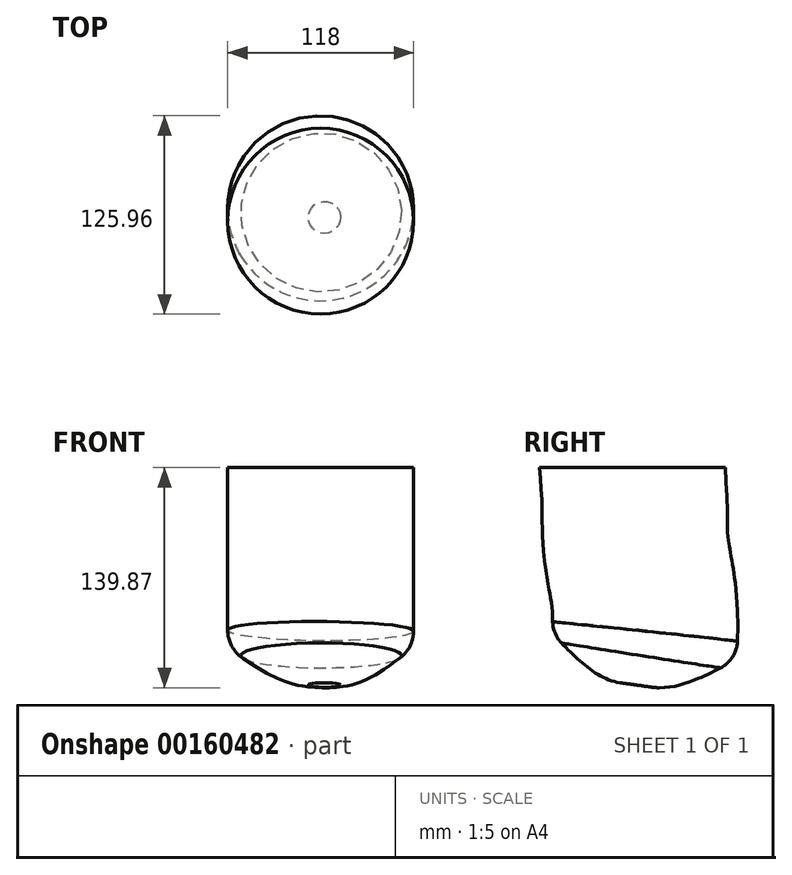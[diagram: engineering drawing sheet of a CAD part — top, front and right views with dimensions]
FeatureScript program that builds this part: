
annotation { "Feature Type Name" : "Feature", "Feature Type Description" : "" }
export const myFeature = defineFeature(function(context is Context, id is Id, definition is map)
    precondition{}
    {
        {
            var Q0;
            Q0=qCreatedBy(makeId("Top.planeOp"),FACE);
            var sketch = newSketch(context, id + "F0", { "sketchPlane" : qUnion([Q0])});
            skCircle(sketch, "E0", {"center": v(0, 0) * mm, "radius": 59 * mm});
            skSolve(sketch);
        }
        {
            var Q0;
            Q0=qCreatedBy(makeId("Right.planeOp"),FACE);
            var sketch = newSketch(context, id + "F1", { "sketchPlane" : qUnion([Q0])});
            skFitSpline(sketch, "E1", {"points": [v(0, 0) * mm, v(1.92, -44.85) * mm, v(5.06, -67.83) * mm, v(7.76, -113.62) * mm], "startDerivative": vector(16.2, -187.33) * mm, "endDerivative": vector(-9.85, -186.66) * mm});
            skSolve(sketch);
        }
        {
            var Q0;
            Q0=makeQuery(id+"F0.imprint","IMPRINT",FACE,{"disambiguationData":[TD([[makeQuery(id+"F0.imprint","IMPRINT",EDGE,{"derivedFrom":sQuery(id+"F0.wireOp",EDGE,"E0")}),1.0]])]});
            var Q1;
            Q1=sQuery(id+"F0.wireOp",EDGE,"E0");
            var Q2;
            Q2=sQuery(id+"F1.wireOp",EDGE,"E1");
            sweep(context, id + "F2", {"profiles" : qUnion([Q0]), "surfaceProfiles" : qUnion([Q1]), "path" : qUnion([Q2])});
        }
        {
            var Q0;
            Q0=makeQuery(id+"F2.opSweep","CAP_FACE",FACE,{"disambiguationData":[OSD([sQuery(id+"F0.wireOp",EDGE,"E0"),sQuery(id+"F1.wireOp",VERTEX,"E1.end")])],"isStart":false});
            cPlane(context, id + "F3", {"entities" : qUnion([Q0]), "cplaneType" : CPlaneType.OFFSET, "offset" : 25 * mm, "width" : 150 * mm, "height" : 150 * mm});
        }
        {
            var Q0;
            Q0=qCreatedBy(id+"F3.planeOp",FACE);
            var sketch = newSketch(context, id + "F4", { "sketchPlane" : qUnion([Q0])});
            skCircle(sketch, "E2", {"center": v(2.45, -21.44) * mm, "radius": 10.25 * mm});
            skSolve(sketch);
        }
        {
            var Q1;
            Q1=makeQuery(id+"F2.opSweep","CAP_FACE",FACE,{"disambiguationData":[OSD([sQuery(id+"F0.wireOp",EDGE,"E0"),sQuery(id+"F1.wireOp",VERTEX,"E1.end")])],"isStart":false});
            var Q2;
            Q2=makeQuery(id+"F4.imprint","IMPRINT",FACE,{"disambiguationData":[TD([[makeQuery(id+"F4.imprint","IMPRINT",EDGE,{"derivedFrom":sQuery(id+"F4.wireOp",EDGE,"E2")}),1.0]])]});
            loft(context, id + "F5", {"operationType" : NewBodyOperationType.ADD, "endCondition" : LoftEndDerivativeType.TANGENT_TO_PROFILE, "endMagnitude" : 1, "sheetProfilesArray" : [{ "sheetProfileEntities" : qUnion([Q1]) }, { "sheetProfileEntities" : qUnion([Q2]) }]});
        }
        {
            var Q0;
            {var subQ0=sQuery(id+"F1.wireOp",VERTEX,"E1.end");var subQ1=sQuery(id+"F0.wireOp",EDGE,"E0");Q0=makeQuery(id+"F5.boolean.opBoolean","MERGE",EDGE,{"derivedFrom":[makeQuery(id+"F2.opSweep","CAP_EDGE",EDGE,{"disambiguationData":[OSD([subQ1,subQ0])],"isStart":false}),makeQuery(id+"F5.opLoft","MID_CAP_EDGE",EDGE,{"disambiguationData":[OSD([subQ1,subQ0])],"capPos":0.0})]});}
            fillet(context, id + "F6", {"entities" : qUnion([Q0]), "radius" : 20 * mm, "tangentPropagation" : true, "allowEdgeOverflow" : false});
        }
    });
